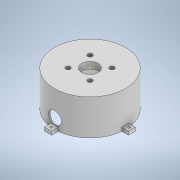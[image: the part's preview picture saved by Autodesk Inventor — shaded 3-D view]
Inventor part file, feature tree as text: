
AUTODESK INVENTOR PART (.ipt)
format: ipt  version: 2021 (Build 250183000, 183)  size: 287,744 bytes
history: native  units: mm
features: sketch x24, extrude x11, plane x6, other x2
ambient origin geometry x8: Origin, YZ Plane, XZ Plane, XY Plane, X Axis, Y Axis, Z Axis, Center Point
bodies: Solid1 (feature_tree)
feature tree (43):
  sketch  "Sketch1"  dims[d3=100.0mm d4=50.0mm d5=0.0mm]
  plane  "Work Plane26"
  extrude  "Base grosor"  Depth=50.0mm TaperAngle=0.0deg
  plane  "Work Plane22"
  extrude  "Base agujero"  Depth=114.0mm TaperAngle=0.0deg
  extrude  "Agujero para cables"  Depth=54.25mm
  other  "Separacion Tapa"
  other  "Separacion Base Motor"
  sketch  "Sketch5"  dims[d232=31.0mm d233=31.0mm]
  sketch  "Sketch6"  dims[d234=3.1mm d235=3.1mm]
  plane  "Work Plane16"
  extrude  "Extrusion59"  Depth=23.0mm
  plane  "Work Plane36"
  extrude  "Extrusion60"  Depth=31.0mm
  extrude  "Extrusion64"  Depth=3.1mm
  plane  "Work Plane42"
  extrude  "Extrusion65"  Depth=3.1mm
  extrude  "Extrusion66"  TaperAngle=0.0deg  [1 undecoded]
  sketch  "Sketch144"  dims[d281=26.5mm d282=0.0mm]
  sketch  "Sketch145"  dims[d283=6.5mm]
  sketch  "Sketch147"  dims[d284=6.5mm]
  sketch  "Sketch148"  dims[d285=6.5mm]
  plane  "Work Plane45"
  extrude  "Extrusion67"  Depth=6.0mm
  extrude  "Extrusion68"  Depth=6.0mm
  sketch  "Sketch151"  dims[d289=-48.25mm]
  extrude  "Extrusion69"  Depth=3.0mm
  sketch  "Sketch153"  dims[d292=10.0mm]
  sketch  "Sketch154"  dims[d293=10.0mm]
  sketch  "Sketch155"  dims[d294=18.0mm]
  sketch  "Sketch156"  dims[d295=18.0mm]
  sketch  "Sketch157"  dims[d296=10.0mm d297=10.0mm d298=18.0mm d299=5.0mm d300=0.0mm d301=3.1mm d302=3.1mm d303=3.1mm d304=3.1mm d305=12.6mm d306=0.0mm d307=89.65mm d308=0.0mm d12=0.872665mm d13=0.5mm d14=0.872665mm d15=0.5mm d16=0.872665mm d17=0.872665mm d18=0.5mm d19=0.872665mm d29=0.5mm d30=0.872665mm d31=0.5mm d32=0.872665mm d53=0.5mm d54=0.872665mm d55=0.5mm d56=0.872665mm d59=0.5mm d60=0.872665mm d61=0.5mm d62=0.872665mm d69=0.5mm d70=0.872665mm d71=0.5mm d72=0.872665mm d116=0.5mm d117=0.872665mm d118=0.5mm d119=0.872665mm d125=0.5mm d126=0.872665mm d127=0.5mm d128=0.872665mm d129=0.872665mm d130=0.5mm d131=0.872665mm d135=0.5mm d136=0.872665mm d137=0.5mm d138=0.872665mm d139=0.5mm d140=0.872665mm d141=0.5mm d142=0.872665mm d173=0.5mm d174=0.872665mm d175=0.5mm d176=0.872665mm d177=0.5mm d178=0.872665mm d179=0.5mm d180=0.872665mm d182=0.5mm d183=0.872665mm d184=0.5mm d185=0.872665mm d197=0.5mm d198=0.872665mm d199=0.5mm d200=0.872665mm d228=0.5mm d240=0.5mm d241=0.872665mm]
  sketch  "Sketch2"  dims[d6=96.0mm d7=114.0mm d8=0.0mm]
  sketch  "Sketch3"  dims[d9=89.75mm d10=0.0mm d11=54.25mm]
  sketch  "Sketch4"  dims[d229=9.5mm d230=0.0mm d231=23.0mm]
  sketch  "Sketch127"  dims[d236=3.1mm d237=3.1mm]
  sketch  "Sketch128"  dims[d238=31.0mm d239=0.0mm]
  sketch  "Sketch140"  dims[d272=6.0mm d273=6.0mm]
  sketch  "Sketch141"  dims[d274=6.0mm d275=6.0mm]
  sketch  "Sketch143"  dims[d276=3.0mm d277=0.0mm d280=18.0mm]
  sketch  "Sketch149"  dims[d286=6.5mm]
  sketch  "Sketch150"  dims[d287=3.0mm d288=0.0mm]
  sketch  "Sketch152"  dims[d291=18.0mm]
note: 1 required parameter value undecoded (feature->parameter linkage not recoverable at this tier; creation-order binding heuristic only, values carry confidence <= 0.55)
